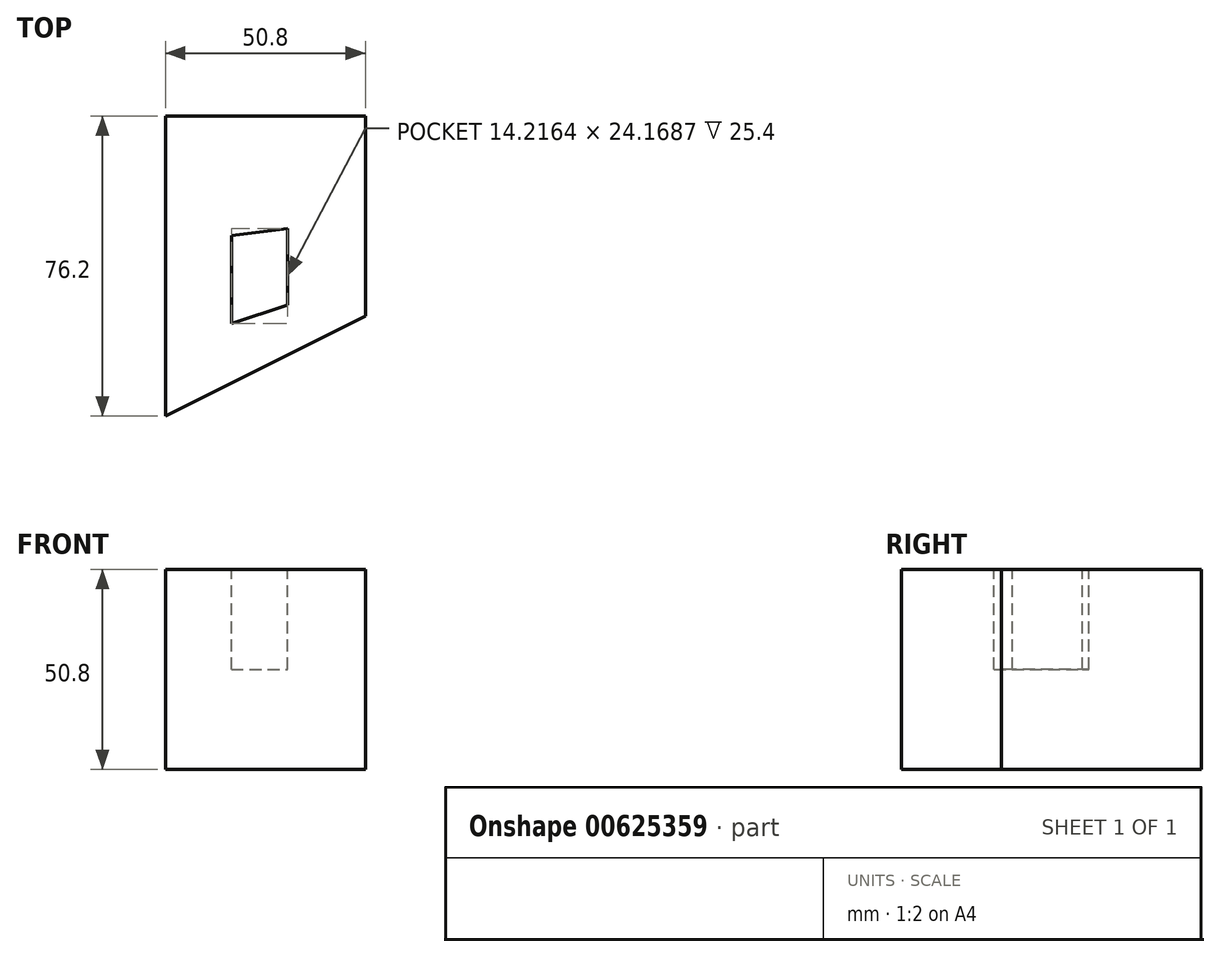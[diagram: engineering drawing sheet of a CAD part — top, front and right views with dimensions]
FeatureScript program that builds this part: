
annotation { "Feature Type Name" : "Feature", "Feature Type Description" : "" }
export const myFeature = defineFeature(function(context is Context, id is Id, definition is map)
    precondition{}
    {
        {
            var Q0;
            Q0=qCreatedBy(makeId("Top.planeOp"),FACE);
            var sketch = newSketch(context, id + "F0", { "sketchPlane" : qUnion([Q0])});
            skLineSegment(sketch, "E0", {"start": v(0, 0) * mm, "end": v(0, 76.2) * mm});
            skLineSegment(sketch, "E1", {"start": v(0, 76.2) * mm, "end": v(50.8, 76.2) * mm});
            skLineSegment(sketch, "E2", {"start": v(50.8, 76.2) * mm, "end": v(50.8, 25.4) * mm});
            skLineSegment(sketch, "E3", {"start": v(50.8, 25.4) * mm, "end": v(0, 0) * mm});
            skSolve(sketch);
        }
        {
            var Q0;
            Q0=makeQuery(id+"F0.imprint","IMPRINT",FACE,{"disambiguationData":[TD([[makeQuery(id+"F0.imprint","IMPRINT",EDGE,{"derivedFrom":sQuery(id+"F0.wireOp",EDGE,"E0")}),-1.0]])]});
            extrude(context, id + "F1", {"entities" : qUnion([Q0]), "depth" : 50.8 * mm, "offsetDistance" : 25.4 * mm});
        }
        {
            var Q0;
            Q0=makeQuery(id+"F1.opExtrude","CAP_FACE",FACE,{"disambiguationData":[OSD([sQuery(id+"F0.wireOp",EDGE,"E0"),sQuery(id+"F0.wireOp",EDGE,"E1"),sQuery(id+"F0.wireOp",EDGE,"E2"),sQuery(id+"F0.wireOp",EDGE,"E3")])],"isStart":false});
            var sketch = newSketch(context, id + "F2", { "sketchPlane" : qUnion([Q0])});
            skLineSegment(sketch, "E4", {"start": v(31, 47.6) * mm, "end": v(31, 28.13) * mm});
            skLineSegment(sketch, "E5", {"start": v(31, 28.13) * mm, "end": v(16.78, 23.43) * mm});
            skLineSegment(sketch, "E6", {"start": v(16.78, 23.43) * mm, "end": v(16.78, 45.88) * mm});
            skLineSegment(sketch, "E7", {"start": v(16.78, 45.88) * mm, "end": v(31, 47.6) * mm});
            skSolve(sketch);
        }
        {
            var Q0;
            Q0 = qSketchRegion(id + "F2", true);
            extrude(context, id + "F3", {"entities" : qUnion([Q0]), "operationType" : NewBodyOperationType.REMOVE, "oppositeDirection" : true, "depth" : 25.4 * mm, "offsetDistance" : 25.4 * mm});
        }
    });
